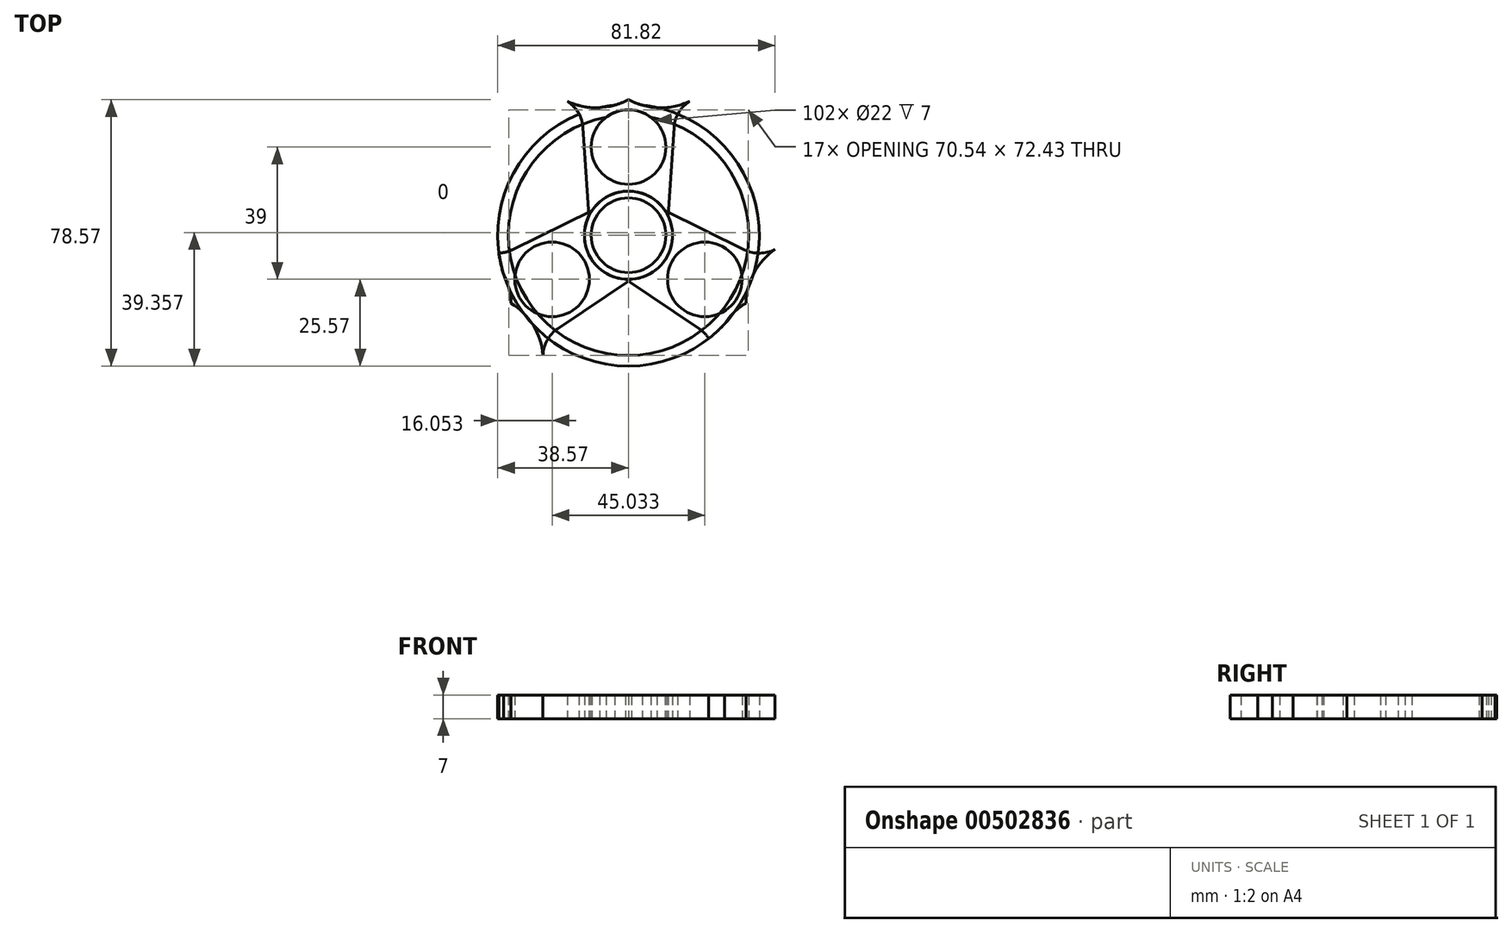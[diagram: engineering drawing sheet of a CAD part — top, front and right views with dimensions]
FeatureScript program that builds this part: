
annotation { "Feature Type Name" : "Feature", "Feature Type Description" : "" }
export const myFeature = defineFeature(function(context is Context, id is Id, definition is map)
    precondition{}
    {
        {
            var Q0;
            Q0=qCreatedBy(makeId("Top.planeOp"),FACE);
            var sketch = newSketch(context, id + "F0", { "sketchPlane" : qUnion([Q0])});
            skCircle(sketch, "E0", {"center": v(0, 0) * mm, "radius": 11 * mm});
            skCircle(sketch, "E1", {"center": v(0, 0) * mm, "radius": 13 * mm});
            skCircle(sketch, "E2", {"center": v(0, 26) * mm, "radius": 11 * mm});
            skLineSegment(sketch, "E3", {"start": v(0, 0) * mm, "end": v(0, 6.9) * mm});
            skLineSegment(sketch, "E4", {"start": v(13.42, 31.76) * mm, "end": v(11.66, 5.76) * mm});
            skLineSegment(sketch, "E5.MirrorCS", {"start": v(-13.42, 31.76) * mm, "end": v(-11.66, 5.76) * mm});
            skArc(sketch, "E6", {"start": v(-13.42, 31.76) * mm, "mid": v(-14.8, 36.2) * mm, "end": v(-18.03, 39.52) * mm});
            skArc(sketch, "E7", {"start": v(-18.03, 39.52) * mm, "mid": v(-8.96, 37.61) * mm, "end": v(0, 40) * mm});
            skArc(sketch, "E8.MirrorCS", {"start": v(13.42, 31.76) * mm, "mid": v(14.8, 36.2) * mm, "end": v(18.03, 39.52) * mm});
            skArc(sketch, "E9.MirrorCS", {"start": v(18.03, 39.52) * mm, "mid": v(8.96, 37.61) * mm, "end": v(0, 40) * mm});
            skCircle(sketch, "E10", {"center": v(0, 0) * mm, "radius": 38.57 * mm});
            skCircle(sketch, "E11", {"center": v(0, 0) * mm, "radius": 35.43 * mm});
            skSolve(sketch);
        }
        {
            var Q0;
            Q0=makeQuery(id+"F0.imprint","IMPRINT",FACE,{"disambiguationData":[TD([[makeQuery(id+"F0.imprint","IMPRINT",EDGE,{"derivedFrom":sQuery(id+"F0.wireOp",EDGE,"smy3A69N-p4BX-sQ8V-GM79-3SxZuGPn2iYk")}),-1.0]])]});
            var Q1;
            Q1=makeQuery(id+"F0.imprint","IMPRINT",FACE,{"disambiguationData":[TD([[makeQuery(id+"F0.imprint","IMPRINT",EDGE,{"derivedFrom":sQuery(id+"F0.wireOp",EDGE,"E0")}),-1.0]])]});
            var Q2;
            Q2=makeQuery(id+"F0.imprint","IMPRINT",FACE,{"disambiguationData":[TD([[makeQuery(id+"F0.imprint","IMPRINT",EDGE,{"derivedFrom":sQuery(id+"F0.wireOp",EDGE,"E2")}),-1.0]])]});
            var Q3;
            {var subQ3=sQuery(id+"F0.wireOp",EDGE,"E11");var subQ5=sQuery(id+"F0.wireOp",EDGE,"E2");var subQ6=makeQuery(id+"F0.imprint","INTERSECT",VERTEX,{"disambiguationData":[OD(0.0)],"derivedFrom":[subQ5,subQ3]});Q3=makeQuery(id+"F0.imprint","IMPRINT",FACE,{"disambiguationData":[TD([[makeQuery(id+"F0.imprint","IMPRINT",EDGE,{"disambiguationData":[TD([[subQ6,-1.0]])],"derivedFrom":subQ5}),-1.0]])]});}
            var Q4;
            {var subQ0=sQuery(id+"F0.wireOp",EDGE,"E7");var subQ1=sQuery(id+"F0.wireOp",EDGE,"E6");var subQ2=makeQuery(id+"F0.imprint","INTERSECT",VERTEX,{"derivedFrom":[subQ1,subQ0]});Q4=makeQuery(id+"F0.imprint","IMPRINT",FACE,{"disambiguationData":[TD([[makeQuery(id+"F0.imprint","IMPRINT",EDGE,{"disambiguationData":[TD([[subQ2,1.0]])],"derivedFrom":subQ1}),-1.0]])]});}
            var Q5;
            {var subQ0=sQuery(id+"F0.wireOp",EDGE,"E9.MirrorCS");var subQ1=sQuery(id+"F0.wireOp",EDGE,"E7");var subQ2=makeQuery(id+"F0.imprint","INTERSECT",VERTEX,{"derivedFrom":[subQ1,subQ0]});Q5=makeQuery(id+"F0.imprint","IMPRINT",FACE,{"disambiguationData":[TD([[makeQuery(id+"F0.imprint","IMPRINT",EDGE,{"disambiguationData":[TD([[subQ2,1.0]])],"derivedFrom":subQ1}),-1.0]])]});}
            var Q6;
            {var subQ0=sQuery(id+"F0.wireOp",EDGE,"E9.MirrorCS");var subQ1=sQuery(id+"F0.wireOp",EDGE,"E8.MirrorCS");var subQ2=makeQuery(id+"F0.imprint","INTERSECT",VERTEX,{"derivedFrom":[subQ1,subQ0]});Q6=makeQuery(id+"F0.imprint","IMPRINT",FACE,{"disambiguationData":[TD([[makeQuery(id+"F0.imprint","IMPRINT",EDGE,{"disambiguationData":[TD([[subQ2,1.0]])],"derivedFrom":subQ1}),1.0]])]});}
            extrude(context, id + "F1", {"entities" : qUnion([Q0, Q1, Q2, Q3, Q4, Q5, Q6]), "endBound" : BoundingType.SYMMETRIC, "depth" : 7 * mm});
        }
        {
            var Q0;
            Q0=makeQuery(id+"F1.opExtrude","SWEPT_BODY",BODY,{"disambiguationData":[OSD([sQuery(id+"F0.wireOp",EDGE,"E0"),sQuery(id+"F0.wireOp",EDGE,"smy3A69N-p4BX-sQ8V-GM79-3SxZuGPn2iYk"),sQuery(id+"F0.wireOp",EDGE,"HrklUpNS-VKmq-E8Wz-JcHh-4kZhRdKcDkxJ"),sQuery(id+"F0.wireOp",EDGE,"VKMo0bLC-QqHn-6hCs-5vkH-h1WAsoLDgrYN"),sQuery(id+"F0.wireOp",EDGE,"KqvMMmtJ-kShb-u1Q6-0jPt-4SRrPrR2BJWt"),sQuery(id+"F0.wireOp",EDGE,"ZxUdskTh-0G7j-2j06-lpIb-P6DuDP8MQo74"),sQuery(id+"F0.wireOp",EDGE,"E1"),sQuery(id+"F0.wireOp",EDGE,"E2")])]});
            var Q1;
            Q1=makeQuery(id+"F1.opExtrude","SWEPT_FACE",FACE,{"disambiguationData":[OSD([sQuery(id+"F0.wireOp",EDGE,"E0")])]});
            circularPattern(context, id + "F2", {"entities" : qUnion([Q0]), "axis" : qUnion([Q1]), "angle" : 360 * degree, "instanceCount" : 3, "equalSpace" : true});
        }
        {
            var Q0;
            Q0 = qSketchRegion(id + "F0", true);
            extrude(context, id + "F3", {"entities" : qUnion([Q0]), "endBound" : BoundingType.SYMMETRIC, "depth" : 7 * mm});
        }
    });
